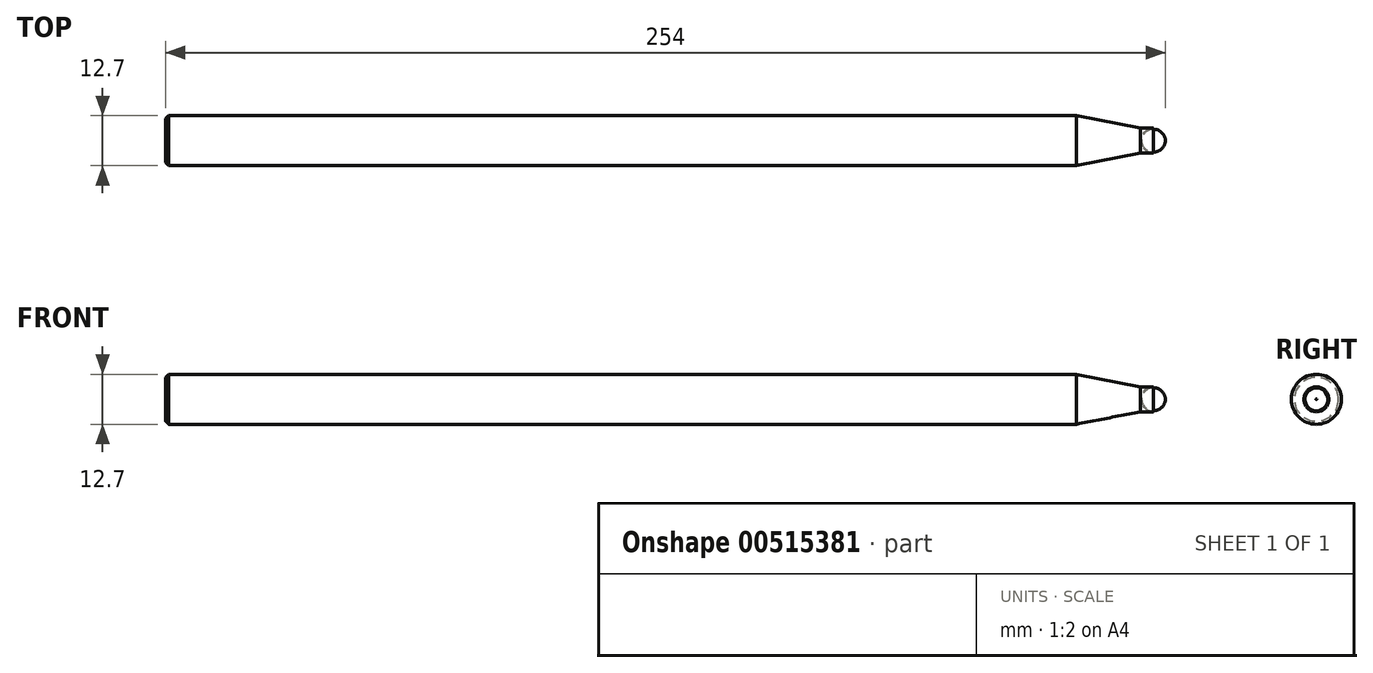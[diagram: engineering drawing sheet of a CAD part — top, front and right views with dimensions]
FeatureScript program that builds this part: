
annotation { "Feature Type Name" : "Feature", "Feature Type Description" : "" }
export const myFeature = defineFeature(function(context is Context, id is Id, definition is map)
    precondition{}
    {
        {
            var Q0;
            Q0=qCreatedBy(makeId("Top.planeOp"),FACE);
            var sketch = newSketch(context, id + "F0", { "sketchPlane" : qUnion([Q0])});
            skLineSegment(sketch, "E0", {"start": v(-219.83, 0) * mm, "end": v(-219.83, 6.35) * mm});
            skLineSegment(sketch, "E1", {"start": v(-219.83, 6.35) * mm, "end": v(11.56, 6.35) * mm});
            skLineSegment(sketch, "E2", {"start": v(34.17, 3.18) * mm, "end": v(34.17, 0) * mm});
            skLineSegment(sketch, "E3", {"start": v(34.17, 0) * mm, "end": v(-219.83, 0) * mm});
            skLineSegment(sketch, "E4", {"start": v(27.82, 3.18) * mm, "end": v(11.56, 6.35) * mm});
            skLineSegment(sketch, "E5", {"start": v(27.82, 3.17) * mm, "end": v(34.17, 3.17) * mm});
            skPoint(sketch, "E5.endSnap0", {"position": v(34.17, 3.18) * mm});
            skPoint(sketch, "E6.orphan", {"position": v(34.17, 6.35) * mm});
            skSolve(sketch);
        }
        {
            var Q0;
            Q0=makeQuery(id+"F0.imprint","IMPRINT",FACE,{"disambiguationData":[TD([[makeQuery(id+"F0.imprint","IMPRINT",EDGE,{"derivedFrom":sQuery(id+"F0.wireOp",EDGE,"E0")}),-1.0]])]});
            var Q1;
            Q1=sQuery(id+"F0.wireOp",EDGE,"E3");
            revolve(context, id + "F1", {"entities" : qUnion([Q0]), "axis" : qUnion([Q1]), "revolveType" : RevolveType.FULL});
        }
        {
            var Q0;
            Q0=makeQuery(id+"F1.opRevolve","SWEPT_EDGE",EDGE,{"disambiguationData":[OSD([sQuery(id+"F0.wireOp",EDGE,"E2"),sQuery(id+"F0.wireOp",EDGE,"E5")])]});
            fillet(context, id + "F2", {"entities" : qUnion([Q0]), "radius" : 3.05 * mm, "tangentPropagation" : true, "allowEdgeOverflow" : false});
        }
        {
            var Q0;
            Q0=makeQuery(id+"F1.opRevolve","SWEPT_EDGE",EDGE,{"disambiguationData":[OSD([sQuery(id+"F0.wireOp",EDGE,"E0"),sQuery(id+"F0.wireOp",EDGE,"E1")])]});
            chamfer(context, id + "F3", {"entities" : qUnion([Q0]), "width" : 0.76 * mm, "tangentPropagation" : true});
        }
    });
